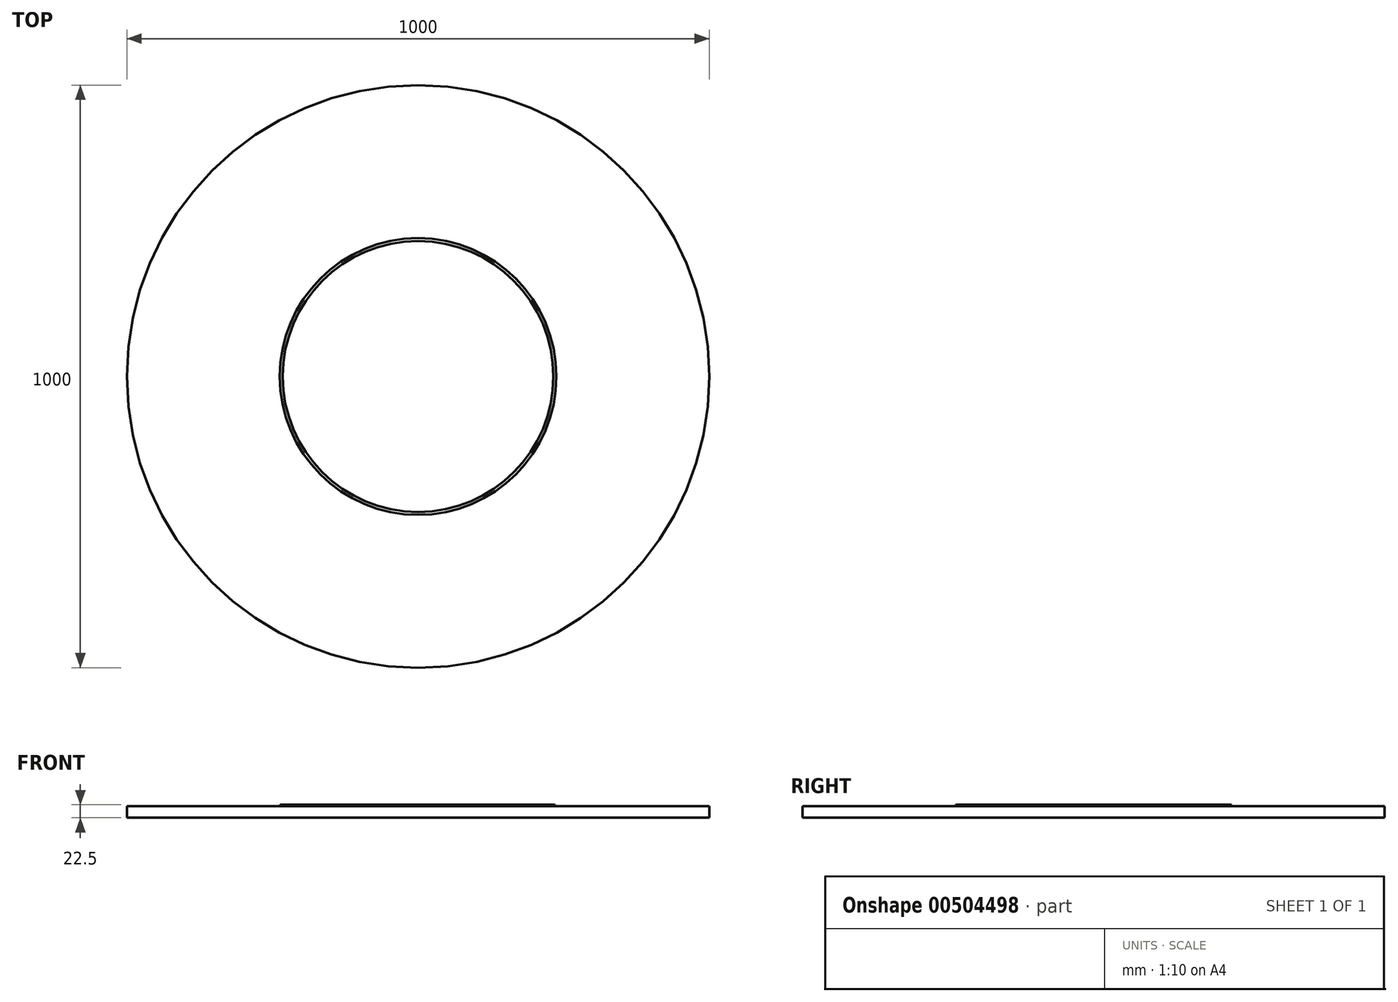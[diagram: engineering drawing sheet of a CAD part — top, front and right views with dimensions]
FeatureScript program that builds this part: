
annotation { "Feature Type Name" : "Feature", "Feature Type Description" : "" }
export const myFeature = defineFeature(function(context is Context, id is Id, definition is map)
    precondition{}
    {
        {
            var Q0;
            Q0=qCreatedBy(makeId("Front.planeOp"),FACE);
            var sketch = newSketch(context, id + "F0", { "sketchPlane" : qUnion([Q0])});
            skLineSegment(sketch, "E0.bottom", {"start": v(0, 0) * mm, "end": v(500, 0) * mm});
            skLineSegment(sketch, "E0.top", {"start": v(0, -20) * mm, "end": v(500, -20) * mm});
            skLineSegment(sketch, "E0.left", {"start": v(0, 0) * mm, "end": v(0, -20) * mm});
            skLineSegment(sketch, "E0.right", {"start": v(500, 0) * mm, "end": v(500, -20) * mm});
            skArc(sketch, "E1", {"start": v(262.5, 0) * mm, "mid": v(265, 2.5) * mm, "end": v(267.5, 0) * mm});
            skSolve(sketch);
        }
        {
            var Q0;
            Q0 = qSketchRegion(id + "F0", true);
            var Q1;
            Q1=sQuery(id+"F0.wireOp",EDGE,"E0.right");
            revolve(context, id + "F1", {"entities" : qUnion([Q0]), "axis" : qUnion([Q1]), "revolveType" : RevolveType.FULL});
        }
        {
            var Q0;
            Q0=qCreatedBy(makeId("Front.planeOp"),FACE);
            var sketch = newSketch(context, id + "F2", { "sketchPlane" : qUnion([Q0])});
            skLineSegment(sketch, "E2", {"start": v(262.5, 0) * mm, "end": v(262.5, 3.5) * mm});
            skLineSegment(sketch, "E3", {"start": v(262.5, 3.5) * mm, "end": v(267.5, 3.5) * mm});
            skLineSegment(sketch, "E4", {"start": v(267.5, 0) * mm, "end": v(267.5, 3.5) * mm});
            skSolve(sketch);
        }
        {
            var Q0;
            Q0=sQuery(id+"F2.wireOp",EDGE,"E3");
            var Q1;
            Q1=sQuery(id+"F2.wireOp",EDGE,"E4");
            var Q2;
            Q2=sQuery(id+"F2.wireOp",EDGE,"E2");
            var Q3;
            Q3=sQuery(id+"F0.wireOp",EDGE,"E0.right");
            revolve(context, id + "F3", {"bodyType" : ToolBodyType.SURFACE, "surfaceEntities" : qUnion([Q0, Q1, Q2]), "axis" : qUnion([Q3]), "revolveType" : RevolveType.FULL});
        }
        {
            var Q0;
            Q0=sQuery(id+"F0.wireOp",EDGE,"E1");
            var Q1;
            Q1=sQuery(id+"F0.wireOp",EDGE,"E0.right");
            revolve(context, id + "F4", {"bodyType" : ToolBodyType.SURFACE, "surfaceEntities" : qUnion([Q0]), "axis" : qUnion([Q1]), "revolveType" : RevolveType.FULL});
        }
    });
